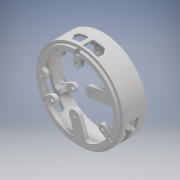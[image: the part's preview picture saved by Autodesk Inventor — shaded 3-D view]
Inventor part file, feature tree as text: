
AUTODESK INVENTOR PART (.ipt)
format: ipt  version: 2018 (Build 220112000, 112)  size: 3,045,888 bytes
history: native  units: mm
features: extrude x14, sketch x13, projected_geometry x9, fillet x8, plane x3, pattern_circular x3, chamfer x2, hole x1
ambient origin geometry x8: Origin, YZ Plane, XZ Plane, XY Plane, X Axis, Y Axis, Z Axis, Center Point
bodies: Solid1 (feature_tree)
feature tree (53):
  sketch  "Sketch1"  dims[d0=0.4mm d1=30.0deg]
  extrude  "Extrusion1"  TaperAngle=30.0deg  [1 undecoded]
  hole  "Hole1"  [1 undecoded]
  extrude  "Extrusion2"  Depth=3.5mm
  extrude  "Extrusion3"  Depth=24.5mm
  extrude  "Extrusion4"  Depth=1.5mm TaperAngle=0.0deg
  extrude  "Extrusion5"  Depth=1.5mm TaperAngle=0.0deg
  extrude  "Extrusion6"  Depth=0.4mm
  fillet  "Fillet1"  Radius=35.0mm
  extrude  "Extrusion7"  Depth=1.5mm
  plane  "Work Plane1"
  extrude  "Extrusion8"  Depth=1.5mm
  pattern_circular  "Circular Pattern1"  [2 undecoded]
  fillet  "Fillet2"  Radius=2.0mm
  fillet  "Fillet3"  Radius=3.0mm
  extrude  "Extrusion9"  Depth=2.0mm
  pattern_circular  "Circular Pattern2"  [2 undecoded]
  chamfer  "Chamfer1"  Distance=54.0mm
  fillet  "Fillet4"  Radius=16.0mm
  fillet  "Fillet5"  Radius=54.0mm
  extrude  "Extrusion10"  Depth=2.0mm
  extrude  "Extrusion11"  Depth=2.0mm
  pattern_circular  "Circular Pattern3"  [2 undecoded]
  chamfer  "Chamfer2"  Distance=54.0mm
  fillet  "Fillet6"  Radius=54.0mm
  plane  "Work Plane2"
  extrude  "Extrusion12"  Depth=4.0mm
  extrude  "Extrusion13"  Depth=2.0mm TaperAngle=0.0deg
  fillet  "Fillet7"  [1 undecoded]
  plane  "Work Plane3"
  extrude  "Extrusion14"  Depth=2.0mm
  fillet  "Fillet8"  Radius=4.0mm
  sketch  "Sketch2"  dims[d2=85.0mm d3=56.0mm]
  projected_geometry  "Projected Loop1"
  sketch  "Sketch3"  dims[d4=52.0mm d5=3.5mm]
  projected_geometry  "Projected Loop2"
  sketch  "Sketch4"  dims[d6=49.0mm d7=24.5mm]
  projected_geometry  "Projected Loop3"
  sketch  "Sketch5"  dims[d8=58.0mm d9=1.5mm d10=0.0mm]
  projected_geometry  "Projected Loop4"
  sketch  "Sketch7"  dims[d11=2.9mm d12=6.0mm d13=5.5mm d14=2.9mm d15=90.0deg d16=8.0mm d17=20.594885mm d18=1.5mm d19=0.0mm]
  sketch  "Sketch8"  dims[d20=35.0mm d21=0.0mm d22=0.4mm d23=35.0mm d24=0.0mm]
  sketch  "Sketch9"  dims[d25=1.5mm d26=1.5mm]
  sketch  "Sketch11"  dims[d27=1.5mm d28=1.5mm]
  projected_geometry  "Projected Loop6"
  sketch  "Sketch12"  dims[d29=4.0mm d30=0.0mm]
  projected_geometry  "Projected Loop7"
  sketch  "Sketch14"  dims[d31=5.5mm]
  projected_geometry  "Projected Loop8"
  sketch  "Sketch15"  dims[d32=5.5mm]
  projected_geometry  "Projected Loop9"
  sketch  "Sketch16"  dims[d33=5.5mm d34=5.5mm d35=2.0mm d36=0.0mm d37=3.0mm d47=54.0mm d49=16.0mm d50=54.0mm d52=16.0mm d53=54.0mm d54=16.0mm d55=8.0mm d56=54.0mm d57=8.0mm d58=54.0mm d59=54.0mm d60=4.0mm d61=2.0mm d62=0.0mm d63=-4.0mm d65=11.0mm d66=4.0mm d67=0.0mm d68=30.0mm d69=360.0deg d71=5.0mm d72=3.0mm d73=3.0mm d74=0.0mm d75=30.0mm d76=360.0deg d78=2.0mm d79=2.0mm d80=45.0deg d81=5.0mm d82=3.0mm d83=2.5mm d84=0.0mm d85=18.0mm d86=8.0mm d87=3.0mm d88=0.0mm d89=3.0mm d90=2.0mm d91=45.0deg d92=2.0mm d93=30.0mm d94=360.0deg d96=90.0deg d97=90.0deg d98=1.5mm d99=1.5mm d100=5.0mm d101=4.0mm d102=4.0mm d104=4.0mm d105=10.0mm d106=10.0mm d107=0.0mm d108=10.0mm d109=0.0mm d110=2.0mm d111=1.0mm d112=18.0mm d113=18.0mm d114=10.0mm d115=0.0mm d116=2.0mm]
  projected_geometry  "Project Cut Edges1"
note: 9 required parameter values undecoded (feature->parameter linkage not recoverable at this tier; creation-order binding heuristic only, values carry confidence <= 0.55)
